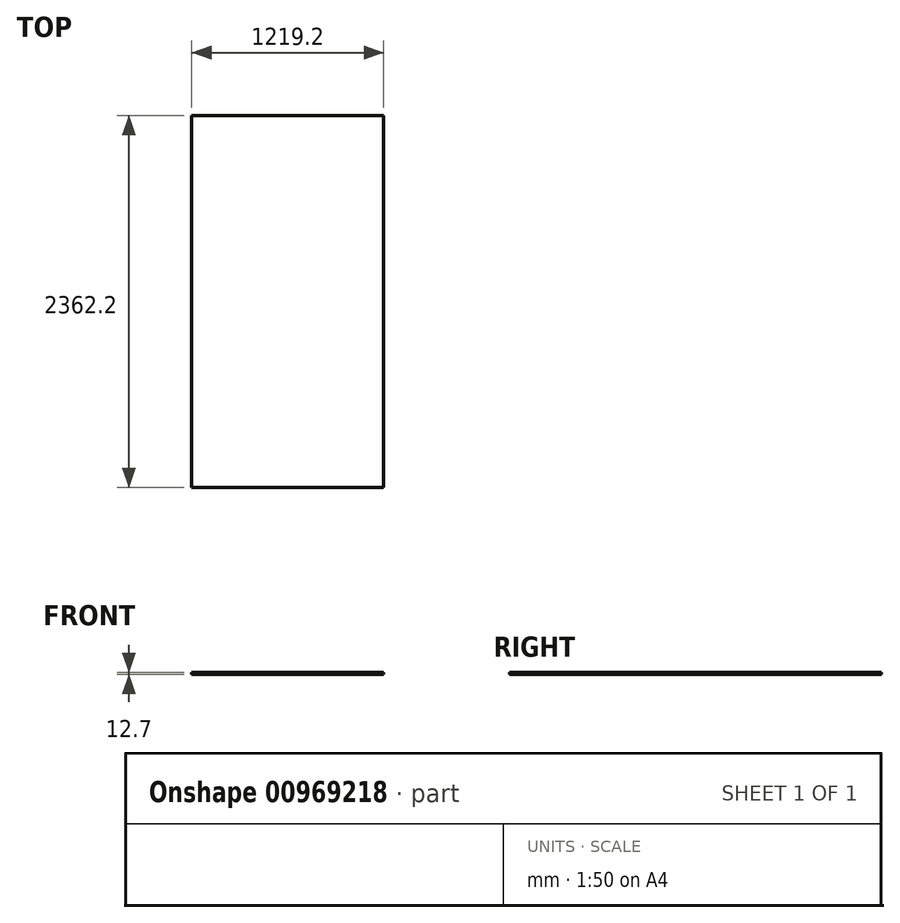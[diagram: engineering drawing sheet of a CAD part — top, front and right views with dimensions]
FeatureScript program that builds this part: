
annotation { "Feature Type Name" : "Feature", "Feature Type Description" : "" }
export const myFeature = defineFeature(function(context is Context, id is Id, definition is map)
    precondition{}
    {
        {
            var Q0;
            Q0=qCreatedBy(makeId("Top.planeOp"),FACE);
            var sketch = newSketch(context, id + "F0", { "sketchPlane" : qUnion([Q0])});
            skLineSegment(sketch, "E0.bottom", {"start": v(-609.6, -1181.1) * mm, "end": v(609.6, -1181.1) * mm});
            skLineSegment(sketch, "E0.top", {"start": v(-609.6, 1181.1) * mm, "end": v(609.6, 1181.1) * mm});
            skLineSegment(sketch, "E0.left", {"start": v(-609.6, -1181.1) * mm, "end": v(-609.6, 1181.1) * mm});
            skLineSegment(sketch, "E0.right", {"start": v(609.6, -1181.1) * mm, "end": v(609.6, 1181.1) * mm});
            skPoint(sketch, "E0.middle", {"position": v(0, 0) * mm});
            skSolve(sketch);
        }
        {
            var Q0;
            Q0 = qSketchRegion(id + "F0", true);
            extrude(context, id + "F1", {"entities" : qUnion([Q0]), "depth" : 12.7 * mm, "offsetDistance" : 25.4 * mm});
        }
    });
